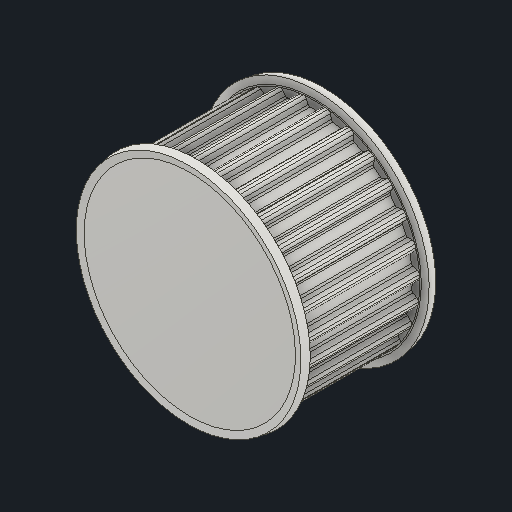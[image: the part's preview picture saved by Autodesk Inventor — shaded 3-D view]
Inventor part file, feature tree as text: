
AUTODESK INVENTOR PART (.ipt)
format: ipt  version: 2023.1 (Build 271208000, 208)  size: 438,272 bytes
history: native  units: mm (DEFAULTED — no unit token found)
features: other x3, extrude x2, fillet x1, pattern_circular x1
ambient origin geometry x8: Origin, YZ Plane, XZ Plane, XY Plane, X Axis, Y Axis, Z Axis, Center Point
bodies: Solid1 (feature_tree)
feature tree (7):
  other  "Pulley Sketch"
  extrude  "Base Body"  Depth=21.485917mm
  extrude  "Tooth"  Depth=0.3mm
  fillet  "Tooth Fillet"  Radius=0.75mm
  pattern_circular  "Teeth"  [2 undecoded]
  other  "Left flange"
  other  "Right flange"
note: 2 required parameter values undecoded (feature->parameter linkage not recoverable at this tier; creation-order binding heuristic only, values carry confidence <= 0.55)
